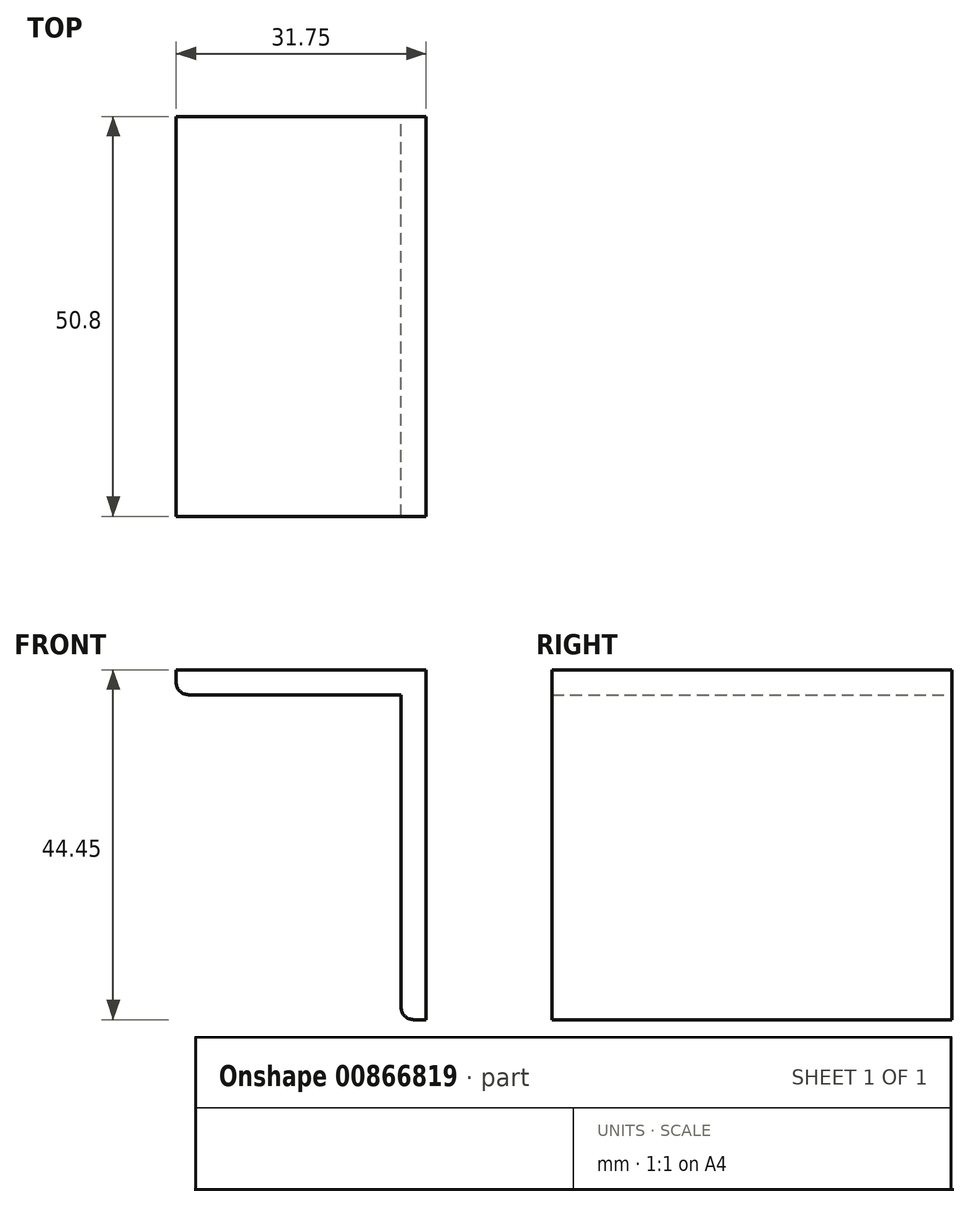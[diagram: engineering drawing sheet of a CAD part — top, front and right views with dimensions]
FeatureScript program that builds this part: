
annotation { "Feature Type Name" : "Feature", "Feature Type Description" : "" }
export const myFeature = defineFeature(function(context is Context, id is Id, definition is map)
    precondition{}
    {
        {
            var Q0;
            Q0=qCreatedBy(makeId("Front.planeOp"),FACE);
            var sketch = newSketch(context, id + "F0", { "sketchPlane" : qUnion([Q0])});
            skLineSegment(sketch, "E0", {"start": v(-78.36, 29.23) * mm, "end": v(-46.61, 29.23) * mm});
            skLineSegment(sketch, "E1", {"start": v(-46.61, 29.23) * mm, "end": v(-46.61, -15.22) * mm});
            skLineSegment(sketch, "E2", {"start": v(-46.61, -15.22) * mm, "end": v(-48.2, -15.22) * mm});
            skLineSegment(sketch, "E3", {"start": v(-49.79, -13.63) * mm, "end": v(-49.79, 26.06) * mm});
            skLineSegment(sketch, "E4", {"start": v(-49.79, 26.06) * mm, "end": v(-76.77, 26.06) * mm});
            skLineSegment(sketch, "E5", {"start": v(-78.36, 27.64) * mm, "end": v(-78.36, 29.23) * mm});
            skPoint(sketch, "E6.visualSharp", {"position": v(-78.36, 26.06) * mm});
            skArc(sketch, "E6.filletArc", {"start": v(-78.36, 27.64) * mm, "mid": v(-77.9, 26.52) * mm, "end": v(-76.77, 26.06) * mm});
            skPoint(sketch, "E7.visualSharp", {"position": v(-49.79, -15.22) * mm});
            skArc(sketch, "E7.filletArc", {"start": v(-49.79, -13.63) * mm, "mid": v(-49.32, -14.75) * mm, "end": v(-48.2, -15.22) * mm});
            skSolve(sketch);
        }
        {
            var Q0;
            Q0=makeQuery(id+"F0.imprint","IMPRINT",FACE,{"disambiguationData":[TD([[makeQuery(id+"F0.imprint","IMPRINT",EDGE,{"derivedFrom":sQuery(id+"F0.wireOp",EDGE,"E0")}),-1.0]])]});
            extrude(context, id + "F1", {"entities" : qUnion([Q0]), "depth" : 50.8 * mm, "offsetDistance" : 25.4 * mm});
        }
    });
